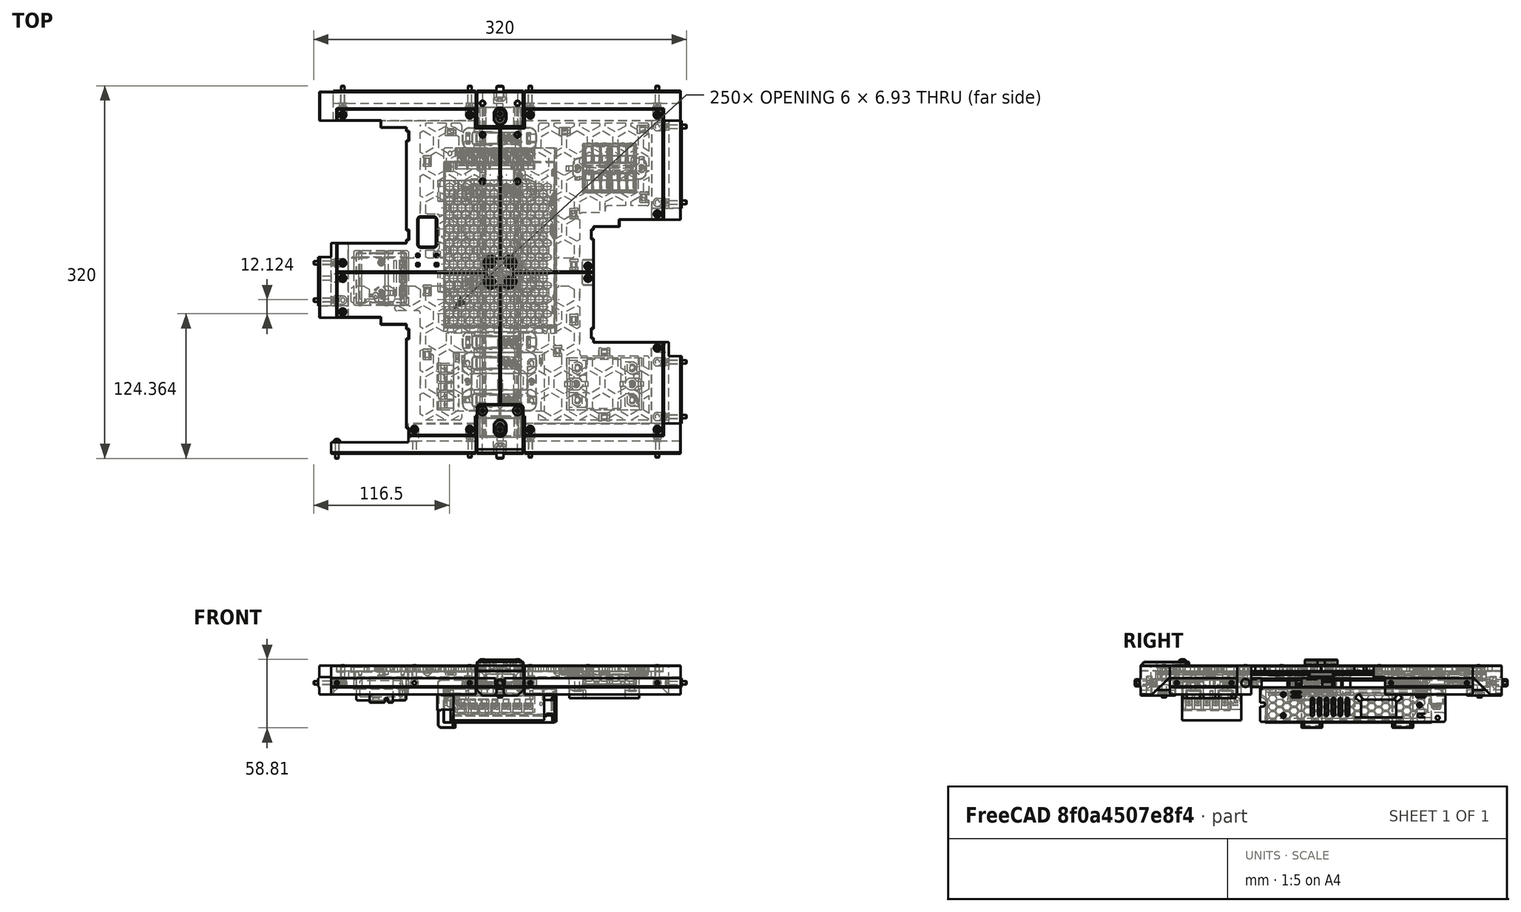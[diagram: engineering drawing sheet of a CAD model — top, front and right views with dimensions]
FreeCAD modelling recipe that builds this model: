
FCSTD DOCUMENT  (FreeCAD 0.19R24291 (Git))
Label: bottom-panel-assembly
License: Other
LicenseURL: GPL3
objects: Part::FeaturePython×53, Part::Feature×38, App::Part×1
note: 91 computed .brp shape members not serialized (recipe doc carries the construction recipe); baked Part::Feature solids carry a one-line shape summary decoded from their .brp

FEATURE [Part::Feature] Chamfer003004002  label="din-end002"
  Placement = pos=(-3.4e-14,-140,0) rot=(0,0,1;3.14159rad)
  shape: bbox 40 x 31 x 21 mm, 75 faces (baked)
FEATURE [Part::Feature] Common001001  label="din-282mm001"
  Placement = pos=(-5e-15,0.5,24.5) rot=(0.707107,0.707107,0;3.14159rad)
  shape: bbox 35 x 282 x 7.5 mm, 66 faces (baked)
FEATURE [Part::Feature] Fusion006002011004053036004001028003005005  label="SSR"
  Placement = pos=(89,-96,2.5) rot=(0.57735,-0.57735,0.57735;4.18879rad)
  shape: bbox 64 x 45 x 22.5 mm, 84 faces (baked)
FEATURE [Part::Feature] Fusion006002011004053036004001028003005006  label="RS-25-5-PSU"
  Placement = pos=(-1,-94,11) rot=(-1,0,0;1.5708rad)
  shape: bbox 91.75 x 51 x 28 mm, 292 faces (baked)
FEATURE [Part::Feature] Fusion006002011004053036004001028003005003  label="PSU-LRS-150-24"
  Placement = pos=(1.29e-14,27,11) rot=(-1,0,0;1.5708rad)
  shape: bbox 97.2 x 159 x 30.02 mm, 3511 faces (baked)
FEATURE [Part::Feature] Fusion006002011004053036004001028003005004  label="SonOff-mini"
  Placement = pos=(-102,-5,10) rot=(0.57735,-0.57735,0.57735;4.18879rad)
  shape: bbox 43.4 x 42.65 x 19.85 mm, 152 faces (baked)
FEATURE [Part::Feature] Cut009001  label="wago-mount-3x4"
  Placement = pos=(95,89,24.5) rot=(0.707107,0.707107,0;3.14159rad)
  shape: bbox 63.6 x 41.99 x 12.2 mm, 224 faces (baked)
FEATURE [Part::Feature] Part__Feature  label="WAGO 222-3c-001"
  Placement = pos=(94,89.5,22.5) rot=(0.57735,-0.57735,0.57735;4.18879rad)
  shape: bbox 22.7 x 21.3 x 9.8 mm, 151 faces (baked)
FEATURE [Part::Feature] Part__Feature001  label="WAGO 222-3c-002"
  Placement = pos=(71.5,89.5,22.5) rot=(0.57735,-0.57735,0.57735;4.18879rad)
  shape: bbox 22.7 x 21.3 x 9.8 mm, 151 faces (baked)
FEATURE [Part::Feature] Part__Feature002  label="WAGO 222-3c-003"
  Placement = pos=(116.7,89.5,22.5) rot=(0.57735,0.57735,-0.57735;4.18879rad)
  shape: bbox 22.7 x 21.3 x 9.8 mm, 151 faces (baked)
FEATURE [Part::Feature] Part__Feature003  label="WAGO 222-3c-004"
  Placement = pos=(94.2,89.5,22.5) rot=(0.57735,0.57735,-0.57735;4.18879rad)
  shape: bbox 22.7 x 21.3 x 9.8 mm, 151 faces (baked)
FEATURE [Part::Feature] Chamfer003001  label="LRS-din-arm001"
  Placement = pos=(16.79,4.5,-5.61) rot=(0,0,1;0rad)
  shape: bbox 28.4 x 18 x 41.6 mm, 61 faces (baked)
FEATURE [Part::Feature] Cut003001  label="LRS-din-mount001"
  Placement = pos=(16.79,4.5,-5.61) rot=(0,0,1;0rad)
  shape: bbox 63.6 x 26.5 x 7.603 mm, 177 faces (baked)
FEATURE [Part::Feature] Cut002015015002  label="LRS-din-mount002"
  Placement = pos=(16.79,82.5,-5.61) rot=(0,0,1;0rad)
  shape: bbox 63.6 x 26.5 x 7.603 mm, 177 faces (baked)
FEATURE [Part::Feature] Chamfer005007002002  label="LRS-din-arm002"
  Placement = pos=(16.79,82.5,-5.61) rot=(0,0,1;0rad)
  shape: bbox 28.4 x 18 x 41.6 mm, 61 faces (baked)
FEATURE [Part::Feature] Fillet001
  Placement = pos=(0,-115,11.39) rot=(0,0,1;0rad)
  shape: bbox 63.6 x 50 x 7.603 mm, 347 faces (baked)
FEATURE [Part::FeaturePython] Screw  label="M4x25-Screw"  # Fasteners workbench fastener (typed FeaturePython)
  Placement = pos=(0,136,27.5) rot=(0,0,1;0rad)
  diameter = 2
  invert = false
  length = 11
  lengthCustom = 25
  matchOuter = true
  offset = 0
  thread = false
  type = 39
FEATURE [Part::FeaturePython] Screw001  label="M4x25-Screw001"  # Fasteners workbench fastener (typed FeaturePython)
  Placement = pos=(-3.4e-14,-135,27.5) rot=(0,0,1;0rad)
  diameter = 2
  invert = false
  length = 11
  lengthCustom = 25
  matchOuter = true
  offset = 0
  thread = false
  type = 39
FEATURE [Part::FeaturePython] Nut001  label="M4-Nut001"  # Fasteners workbench fastener (typed FeaturePython)
  Placement = pos=(-3.4e-14,-136,7) rot=(1,0,0;3.14159rad)
  baseObject = -> Chamfer003004002 [Edge141]
  diameter = 6
  invert = true
  matchOuter = true
  offset = 0
  thread = false
  type = 9
FEATURE [Part::FeaturePython] Screw002  label="M3x10-Screw"  # Fasteners workbench fastener (typed FeaturePython)
  Placement = pos=(-73.5,-135,28.5) rot=(0,0,1;0rad)
  diameter = 1
  invert = false
  length = 9
  lengthCustom = 10
  matchOuter = true
  offset = 0
  thread = false
  type = 39
FEATURE [Part::FeaturePython] Screw003  label="M3x10-Screw027"  # Fasteners workbench fastener (typed FeaturePython)
  Placement = pos=(-26,-135,28.5) rot=(0,0,1;0rad)
  diameter = 1
  invert = false
  length = 9
  lengthCustom = 10
  matchOuter = true
  offset = 0
  thread = false
  type = 39
FEATURE [Part::FeaturePython] Screw004  label="M3x10-Screw028"  # Fasteners workbench fastener (typed FeaturePython)
  Placement = pos=(26,-135,28.5) rot=(0,0,1;0rad)
  diameter = 1
  invert = false
  length = 9
  lengthCustom = 10
  matchOuter = true
  offset = 0
  thread = false
  type = 39
FEATURE [Part::FeaturePython] Screw005  label="M3x10-Screw029"  # Fasteners workbench fastener (typed FeaturePython)
  Placement = pos=(135,-135,28.5) rot=(0,0,1;0rad)
  diameter = 1
  invert = false
  length = 9
  lengthCustom = 10
  matchOuter = true
  offset = 0
  thread = false
  type = 39
FEATURE [Part::FeaturePython] Screw006  label="M3x10-Screw018"  # Fasteners workbench fastener (typed FeaturePython)
  Placement = pos=(135,-65,28.5) rot=(0,0,1;0rad)
  diameter = 1
  invert = false
  length = 9
  lengthCustom = 10
  matchOuter = true
  offset = 0
  thread = false
  type = 39
FEATURE [Part::FeaturePython] Screw007  label="M3x10-Screw017"  # Fasteners workbench fastener (typed FeaturePython)
  Placement = pos=(135,50,28.5) rot=(0,0,1;0rad)
  diameter = 1
  invert = false
  length = 9
  lengthCustom = 10
  matchOuter = true
  offset = 0
  thread = false
  type = 39
FEATURE [Part::FeaturePython] Screw008  label="M3x10-Screw023"  # Fasteners workbench fastener (typed FeaturePython)
  Placement = pos=(135,135,28.5) rot=(0,0,1;0rad)
  diameter = 1
  invert = false
  length = 9
  lengthCustom = 10
  matchOuter = true
  offset = 0
  thread = false
  type = 39
FEATURE [Part::FeaturePython] Screw009  label="M3x10-Screw020"  # Fasteners workbench fastener (typed FeaturePython)
  Placement = pos=(26,135,28.5) rot=(0,0,1;0rad)
  diameter = 1
  invert = false
  length = 9
  lengthCustom = 10
  matchOuter = true
  offset = 0
  thread = false
  type = 39
FEATURE [Part::FeaturePython] Screw010  label="M3x10-Screw019"  # Fasteners workbench fastener (typed FeaturePython)
  Placement = pos=(-26,135,28.5) rot=(0,0,1;0rad)
  diameter = 1
  invert = false
  length = 9
  lengthCustom = 10
  matchOuter = true
  offset = 0
  thread = false
  type = 39
FEATURE [Part::FeaturePython] Screw011  label="M3x10-Screw021"  # Fasteners workbench fastener (typed FeaturePython)
  Placement = pos=(-135,135,28.5) rot=(0,0,1;0rad)
  diameter = 1
  invert = false
  length = 9
  lengthCustom = 10
  matchOuter = true
  offset = 0
  thread = false
  type = 39
FEATURE [Part::FeaturePython] Screw012  label="M3x10-Screw024"  # Fasteners workbench fastener (typed FeaturePython)
  Placement = pos=(-135,-34,28.5) rot=(0,0,1;0rad)
  diameter = 1
  invert = false
  length = 9
  lengthCustom = 10
  matchOuter = true
  offset = 0
  thread = false
  type = 39
FEATURE [Part::FeaturePython] Screw013  label="M3x10-Screw025"  # Fasteners workbench fastener (typed FeaturePython)
  Placement = pos=(-135,8,28.5) rot=(0,0,1;0rad)
  diameter = 1
  invert = false
  length = 9
  lengthCustom = 10
  matchOuter = true
  offset = 0
  thread = false
  type = 39
FEATURE [Part::FeaturePython] Screw014  label="M3x15-Screw"  # Fasteners workbench fastener (typed FeaturePython)
  Placement = pos=(135,145,15) rot=(1,0,0;1.5708rad)
  diameter = 4
  invert = true
  length = 10
  lengthCustom = 15
  matchOuter = true
  offset = 0
  thread = false
  type = 33
FEATURE [Part::FeaturePython] Screw015  label="M3x15-Screw025"  # Fasteners workbench fastener (typed FeaturePython)
  Placement = pos=(26,145,15) rot=(1,0,0;1.5708rad)
  diameter = 4
  invert = true
  length = 10
  lengthCustom = 15
  matchOuter = true
  offset = 0
  thread = false
  type = 33
FEATURE [Part::FeaturePython] Screw018  label="M3x15-Screw024"  # Fasteners workbench fastener (typed FeaturePython)
  Placement = pos=(-145,8,15) rot=(0,1,0;1.5708rad)
  diameter = 4
  invert = true
  length = 10
  lengthCustom = 15
  matchOuter = true
  offset = 0
  thread = false
  type = 33
FEATURE [Part::FeaturePython] Screw019  label="M3x15-Screw023"  # Fasteners workbench fastener (typed FeaturePython)
  Placement = pos=(-145,-24,15) rot=(0,1,0;1.5708rad)
  diameter = 4
  invert = true
  length = 10
  lengthCustom = 15
  matchOuter = true
  offset = 0
  thread = false
  type = 33
FEATURE [Part::FeaturePython] Screw020  label="M3x15-Screw022"  # Fasteners workbench fastener (typed FeaturePython)
  Placement = pos=(-26,145,15) rot=(1,0,0;1.5708rad)
  diameter = 4
  invert = true
  length = 10
  lengthCustom = 15
  matchOuter = true
  offset = 0
  thread = false
  type = 33
FEATURE [Part::FeaturePython] Screw021  label="M3x15-Screw021"  # Fasteners workbench fastener (typed FeaturePython)
  Placement = pos=(-135,145,15) rot=(1,0,0;1.5708rad)
  diameter = 4
  invert = true
  length = 10
  lengthCustom = 15
  matchOuter = true
  offset = 0
  thread = false
  type = 33
FEATURE [Part::FeaturePython] Screw023  label="M3x15-Screw028"  # Fasteners workbench fastener (typed FeaturePython)
  Placement = pos=(-26,-144,15) rot=(-1,0,0;1.5708rad)
  diameter = 4
  invert = true
  length = 10
  lengthCustom = 15
  matchOuter = true
  offset = 0
  thread = false
  type = 33
FEATURE [Part::FeaturePython] Screw024  label="M3x15-Screw031"  # Fasteners workbench fastener (typed FeaturePython)
  Placement = pos=(135,-144,15) rot=(-1,0,0;1.5708rad)
  diameter = 4
  invert = true
  length = 10
  lengthCustom = 15
  matchOuter = true
  offset = 0
  thread = false
  type = 33
FEATURE [Part::FeaturePython] Screw025  label="M3x15-Screw030"  # Fasteners workbench fastener (typed FeaturePython)
  Placement = pos=(26,-144,15) rot=(-1,0,0;1.5708rad)
  diameter = 4
  invert = true
  length = 10
  lengthCustom = 15
  matchOuter = true
  offset = 0
  thread = false
  type = 33
FEATURE [Part::FeaturePython] Screw026  label="M3x15-Screw029"  # Fasteners workbench fastener (typed FeaturePython)
  Placement = pos=(-140,-145,15) rot=(-1,0,0;1.5708rad)
  diameter = 1
  invert = true
  length = 9
  lengthCustom = 15
  matchOuter = true
  offset = 0
  thread = false
  type = 39
FEATURE [Part::FeaturePython] Screw029  label="M3x15-Screw027"  # Fasteners workbench fastener (typed FeaturePython)
  Placement = pos=(145,60,15) rot=(0,-1,0;1.5708rad)
  diameter = 4
  invert = true
  length = 10
  lengthCustom = 15
  matchOuter = true
  offset = 0
  thread = false
  type = 33
FEATURE [Part::FeaturePython] Screw030  label="M3x15-Screw026"  # Fasteners workbench fastener (typed FeaturePython)
  Placement = pos=(145,125,15) rot=(0,-1,0;1.5708rad)
  diameter = 4
  invert = true
  length = 10
  lengthCustom = 15
  matchOuter = true
  offset = 0
  thread = false
  type = 33
FEATURE [Part::FeaturePython] Screw031  label="M3x15-Screw033"  # Fasteners workbench fastener (typed FeaturePython)
  Placement = pos=(145,-124,15) rot=(0,-1,0;1.5708rad)
  diameter = 4
  invert = true
  length = 10
  lengthCustom = 15
  matchOuter = true
  offset = 0
  thread = false
  type = 33
FEATURE [Part::FeaturePython] Screw032  label="M3x15-Screw032"  # Fasteners workbench fastener (typed FeaturePython)
  Placement = pos=(145,-77,15) rot=(0,-1,0;1.5708rad)
  diameter = 4
  invert = true
  length = 10
  lengthCustom = 15
  matchOuter = true
  offset = 0
  thread = false
  type = 33
FEATURE [Part::FeaturePython] Screw033  label="M3x6-Screw"  # Fasteners workbench fastener (typed FeaturePython)
  Placement = pos=(66.5,89,21.5) rot=(1,0,0;3.14159rad)
  baseObject = -> Cut009001 [Edge435]
  diameter = 1
  invert = false
  length = 0
  lengthCustom = 6
  matchOuter = true
  offset = 0
  thread = false
  type = 39
FEATURE [Part::FeaturePython] Screw034  label="M3x6-Screw001"  # Fasteners workbench fastener (typed FeaturePython)
  Placement = pos=(121.5,89,21.5) rot=(1,0,0;3.14159rad)
  baseObject = -> Cut009001 [Edge192]
  diameter = 1
  invert = false
  length = 0
  lengthCustom = 6
  matchOuter = true
  offset = 0
  thread = false
  type = 39
FEATURE [Part::FeaturePython] Screw035  label="M3x6-Screw019"  # Fasteners workbench fastener (typed FeaturePython)
  Placement = pos=(-102,-18,21.5) rot=(1,0,0;3.14159rad)
  diameter = 1
  invert = false
  length = 0
  lengthCustom = 6
  matchOuter = true
  offset = 0
  thread = false
  type = 39
FEATURE [Part::FeaturePython] Screw036  label="M3x6-Screw018"  # Fasteners workbench fastener (typed FeaturePython)
  Placement = pos=(-102,8.5,21.5) rot=(1,0,0;3.14159rad)
  diameter = 1
  invert = false
  length = 0
  lengthCustom = 6
  matchOuter = true
  offset = 0
  thread = false
  type = 39
FEATURE [Part::FeaturePython] Washer  label="M3-Washer"  # Fasteners workbench fastener (typed FeaturePython)
  Placement = pos=(65.4176,-96,21.5) rot=(1,0,0;3.14159rad)
  baseObject = -> Fusion006002011004053036004001028003005005 [Edge152]
  diameter = 4
  invert = false
  matchOuter = true
  offset = 0
  type = 5
FEATURE [Part::FeaturePython] Washer001  label="M3-Washer001"  # Fasteners workbench fastener (typed FeaturePython)
  Placement = pos=(113.418,-96,21.5) rot=(1,0,0;3.14159rad)
  baseObject = -> Fusion006002011004053036004001028003005005 [Edge76]
  diameter = 4
  invert = false
  matchOuter = true
  offset = 0
  type = 5
FEATURE [Part::FeaturePython] Screw037  label="M3x6-Screw004"  # Fasteners workbench fastener (typed FeaturePython)
  Placement = pos=(65.4176,-96,20.95) rot=(1,0,0;3.14159rad)
  baseObject = -> Washer [Edge1]
  diameter = 1
  invert = false
  length = 0
  lengthCustom = 6
  matchOuter = true
  offset = 0
  thread = false
  type = 39
FEATURE [Part::FeaturePython] Screw038  label="M3x6-Screw005"  # Fasteners workbench fastener (typed FeaturePython)
  Placement = pos=(113.418,-96,20.95) rot=(1,0,0;3.14159rad)
  baseObject = -> Washer001 [Edge1]
  diameter = 1
  invert = false
  length = 0
  lengthCustom = 6
  matchOuter = true
  offset = 0
  thread = false
  type = 39
FEATURE [Part::FeaturePython] Screw039  label="M3x10-Screw012"  # Fasteners workbench fastener (typed FeaturePython)
  Placement = pos=(27,-94,17.99) rot=(0,0,1;0rad)
  baseObject = -> Fillet001 [Edge121]
  diameter = 4
  invert = false
  length = 10
  lengthCustom = 10
  matchOuter = true
  offset = 0
  thread = false
  type = 33
FEATURE [Part::FeaturePython] Screw040  label="M3x10-Screw013"  # Fasteners workbench fastener (typed FeaturePython)
  Placement = pos=(-28,-94,17.99) rot=(0,0,1;0rad)
  baseObject = -> Fillet001 [Edge128]
  diameter = 4
  invert = false
  length = 10
  lengthCustom = 10
  matchOuter = true
  offset = 0
  thread = false
  type = 33
FEATURE [Part::FeaturePython] Screw041  label="M3x6-Screw006"  # Fasteners workbench fastener (typed FeaturePython)
  Placement = pos=(16.79,4.5,13.39) rot=(0,0,1;0rad)
  baseObject = -> Cut003001 [Edge407]
  diameter = 1
  invert = false
  length = 0
  lengthCustom = 6
  matchOuter = true
  offset = 0
  thread = false
  type = 39
FEATURE [Part::FeaturePython] Screw042  label="M3x6-Screw007"  # Fasteners workbench fastener (typed FeaturePython)
  Placement = pos=(16.79,82.5,13.39) rot=(0,0,1;0rad)
  baseObject = -> Cut002015015002 [Edge407]
  diameter = 1
  invert = false
  length = 0
  lengthCustom = 6
  matchOuter = true
  offset = 0
  thread = false
  type = 39
FEATURE [Part::FeaturePython] Screw044  label="M6x10-Screw001"  # Fasteners workbench fastener (typed FeaturePython)
  Placement = pos=(-3.4e-14,-150,15) rot=(-1,0,0;1.5708rad)
  baseObject = -> Chamfer003004002 [Edge49]
  diameter = 4
  invert = true
  length = 0
  lengthCustom = 10
  matchOuter = true
  offset = 0
  thread = false
  type = 39
FEATURE [Part::Feature] Cut001001
  Placement = pos=(0,-140,25) rot=(0,0,1;0rad)
  shape: bbox 40 x 41.5 x 9 mm, 50 faces (baked)
FEATURE [Part::Feature] Cut002015026005020007004001
  Placement = pos=(0,0,30) rot=(0,0,1;0rad)
  shape: bbox 22 x 22 x 3 mm, 24 faces (baked)
FEATURE [Part::Feature] Chamfer005007002031007001
  shape: bbox 26 x 64 x 25 mm, 34 faces (baked)
FEATURE [Part::Feature] Chamfer005007002031007002
  shape: bbox 134 x 26 x 25 mm, 30 faces (baked)
FEATURE [Part::Feature] Chamfer005007002031007003
  shape: bbox 26 x 85 x 25 mm, 28 faces (baked)
FEATURE [Part::Feature] Chamfer005007002031007004
  shape: bbox 134 x 26 x 25 mm, 28 faces (baked)
FEATURE [Part::Feature] Chamfer005007002031007006
  Placement = pos=(0,-1,0) rot=(0,0,1;0rad)
  shape: bbox 134 x 26 x 25 mm, 28 faces (baked)
FEATURE [Part::Feature] Chamfer003001001  label="din-end001"
  Placement = pos=(0,140,0) rot=(0,0,1;0rad)
  shape: bbox 40 x 31 x 21 mm, 75 faces (baked)
FEATURE [Part::FeaturePython] Nut  label="M4-Nut"  # Fasteners workbench fastener (typed FeaturePython)
  Placement = pos=(0,136,7) rot=(1,0,0;3.14159rad)
  baseObject = -> Chamfer003001001 [Edge141]
  diameter = 6
  invert = true
  matchOuter = true
  offset = 0
  thread = false
  type = 9
FEATURE [Part::FeaturePython] Screw045  label="M6x10-Screw"  # Fasteners workbench fastener (typed FeaturePython)
  Placement = pos=(0,150,15) rot=(1,0,0;1.5708rad)
  baseObject = -> Chamfer003001001 [Edge49]
  diameter = 4
  invert = true
  length = 0
  lengthCustom = 10
  matchOuter = true
  offset = 0
  thread = false
  type = 39
FEATURE [Part::FeaturePython] Screw046  label="M3x10-Screw026"  # Fasteners workbench fastener (typed FeaturePython)
  Placement = pos=(-135,-5,28.5) rot=(0,0,1;0rad)
  diameter = 1
  invert = false
  length = 9
  lengthCustom = 10
  matchOuter = true
  offset = 0
  thread = false
  type = 39
FEATURE [Part::Feature] Chamfer005007002029001001001
  Placement = pos=(0,-1,0) rot=(0,0,1;0rad)
  shape: bbox 124 x 26 x 25 mm, 28 faces (baked)
FEATURE [Part::FeaturePython] Screw047  label="M3x6-Screw008"  # Fasteners workbench fastener (typed FeaturePython)
  Placement = pos=(-7,-7,33) rot=(0,0,1;0rad)
  baseObject = -> Cut002015026005020007004001 [Edge41]
  diameter = 1
  invert = false
  length = 0
  lengthCustom = 6
  matchOuter = true
  offset = 0
  thread = false
  type = 39
FEATURE [Part::FeaturePython] Screw048  label="M3x6-Screw009"  # Fasteners workbench fastener (typed FeaturePython)
  Placement = pos=(-7,7,33) rot=(0,0,1;0rad)
  baseObject = -> Cut002015026005020007004001 [Edge42]
  diameter = 1
  invert = false
  length = 0
  lengthCustom = 6
  matchOuter = true
  offset = 0
  thread = false
  type = 39
FEATURE [Part::FeaturePython] Screw049  label="M3x6-Screw010"  # Fasteners workbench fastener (typed FeaturePython)
  Placement = pos=(7,-7,33) rot=(0,0,1;0rad)
  baseObject = -> Cut002015026005020007004001 [Edge39]
  diameter = 1
  invert = false
  length = 0
  lengthCustom = 6
  matchOuter = true
  offset = 0
  thread = false
  type = 39
FEATURE [Part::FeaturePython] Screw050  label="M3x6-Screw011"  # Fasteners workbench fastener (typed FeaturePython)
  Placement = pos=(7,7,33) rot=(0,0,1;0rad)
  baseObject = -> Cut002015026005020007004001 [Edge40]
  diameter = 1
  invert = false
  length = 0
  lengthCustom = 6
  matchOuter = true
  offset = 0
  thread = false
  type = 39
FEATURE [Part::Feature] Cut002015026005020007004002
  Placement = pos=(75.5,0,20) rot=(0,0,1;0rad)
  shape: bbox 10 x 22 x 5 mm, 28 faces (baked)
FEATURE [Part::FeaturePython] Screw051  label="M3x6-Screw016"  # Fasteners workbench fastener (typed FeaturePython)
  Placement = pos=(75.5,-5.25,28.5) rot=(0,0,1;0rad)
  diameter = 1
  invert = false
  length = 0
  lengthCustom = 6
  matchOuter = true
  offset = 0
  thread = false
  type = 39
FEATURE [Part::FeaturePython] Screw052  label="M3x6-Screw017"  # Fasteners workbench fastener (typed FeaturePython)
  Placement = pos=(75.5,5.25,28.5) rot=(0,0,1;0rad)
  diameter = 1
  invert = false
  length = 0
  lengthCustom = 6
  matchOuter = true
  offset = 0
  thread = false
  type = 39
FEATURE [Part::Feature] Fusion006002011004053036004001028003005014018035002001
  shape: bbox 26 x 70 x 25 mm, 29 faces (baked)
FEATURE [Part::FeaturePython] Screw053  label="M4x8-Screw"  # Fasteners workbench fastener (typed FeaturePython)
  Placement = pos=(-15,-119,33) rot=(0,0,1;0rad)
  baseObject = -> Cut001001 [Edge44]
  diameter = 2
  invert = false
  length = 1
  lengthCustom = 8
  matchOuter = true
  offset = 0
  thread = false
  type = 39
FEATURE [Part::FeaturePython] Screw054  label="M4x8-Screw001"  # Fasteners workbench fastener (typed FeaturePython)
  Placement = pos=(15,-119,33) rot=(0,0,1;0rad)
  baseObject = -> Cut001001 [Edge45]
  diameter = 2
  invert = false
  length = 1
  lengthCustom = 8
  matchOuter = true
  offset = 0
  thread = false
  type = 39
FEATURE [Part::Feature] Chamfer005007002031011003003
  Placement = pos=(0,0,0.5) rot=(0,0,1;0rad)
  shape: bbox 139.8 x 139.8 x 8.5 mm, 353 faces (baked)
FEATURE [Part::Feature] Chamfer005007002031008001
  Placement = pos=(0,0,0.5) rot=(0,0,1;0rad)
  shape: bbox 139.8 x 139.8 x 8.5 mm, 330 faces (baked)
FEATURE [Part::Feature] Chamfer005007002031011003004
  Placement = pos=(0,0,0.5) rot=(0,0,1;0rad)
  shape: bbox 139.8 x 139.8 x 8.5 mm, 275 faces (baked)
FEATURE [Part::Feature] Chamfer005007002031009001
  Placement = pos=(0,0,0.5) rot=(0,0,1;0rad)
  shape: bbox 139.8 x 139.8 x 8.5 mm, 425 faces (baked)
FEATURE [Part::Feature] Cut002001001
  Placement = pos=(-102,-4.75,24.5) rot=(0.707107,-0.707107,0;3.14159rad)
  shape: bbox 47 x 47 x 26.5 mm, 108 faces (baked)
FEATURE [Part::Feature] Cut001003001001  label="alt-front-joint"
  Placement = pos=(0,-117,0) rot=(0,0,1;0rad)
  shape: bbox 40 x 41.5 x 9 mm, 50 faces (baked)
FEATURE [Part::Feature] Chamfer001001001  label="alt-middle-joint"
  Placement = pos=(0,0,30) rot=(0,0,1;0rad)
  shape: bbox 27.9 x 27.9 x 5 mm, 50 faces (baked)
FEATURE [Part::Feature] Chamfer005007002031011003005  label="alt-side-joint"
  Placement = pos=(75.5,0,20) rot=(0,0,1;0rad)
  shape: bbox 10 x 22 x 5 mm, 32 faces (baked)
FEATURE [Part::Feature] Chamfer005007002029002004001
  Placement = pos=(0,140,0) rot=(0,0,1;0rad)
  shape: bbox 40 x 30 x 6 mm, 55 faces (baked)
FEATURE [Part::Feature] Cut026001  label="din-wire-mounter"
  Placement = pos=(-0.5,115,23.5) rot=(-0.707107,-0.707107,0;3.14159rad)
  shape: bbox 63.6 x 18 x 7.6 mm, 203 faces (baked)
FEATURE [Part::Feature] Cut002015026005020007004003  label="din-wire-mounter001"
  Placement = pos=(-0.5,-60,23.5) rot=(0.707107,0.707107,0;3.14159rad)
  shape: bbox 63.6 x 18 x 7.6 mm, 203 faces (baked)
FEATURE [App::Part] Part  label="bottom-panel"
  Group = -> [Chamfer003001001,Chamfer003004002,Common001001,Fusion006002011004053036004001028003005005,Fusion006002011004053036004001028003005006,Fusion006002011004053036004001028003005003,Fusion006002011004053036004001028003005004,Cut009001,Part__Feature,Part__Feature001,Part__Feature002,Part__Feature003,Chamfer003001,Cut003001,Cut002015015002,Chamfer005007002002,Fillet001,Screw,Screw001,Nut,Nut001,Screw013,+69 more]
  Origin = -> Origin
